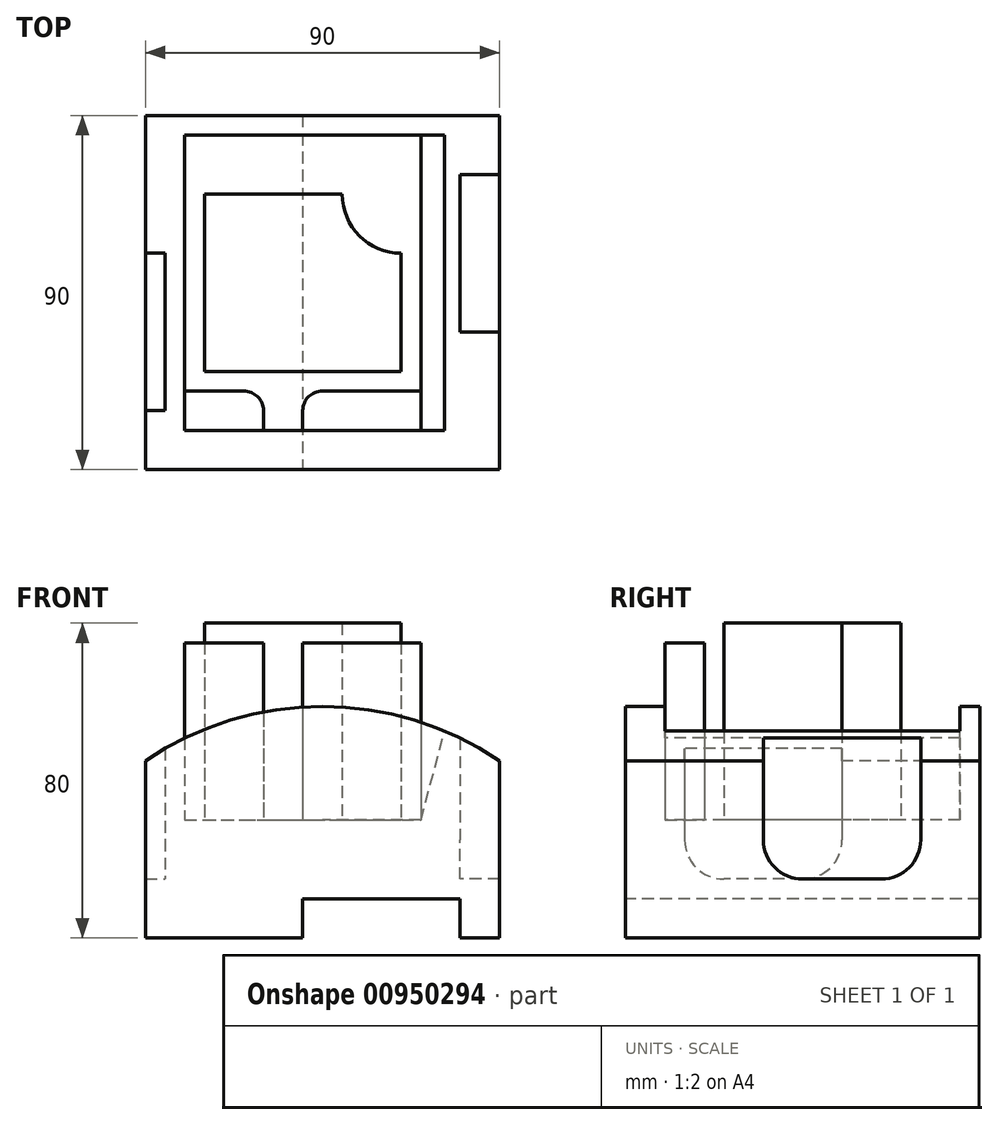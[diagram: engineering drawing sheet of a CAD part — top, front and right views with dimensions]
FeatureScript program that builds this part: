
annotation { "Feature Type Name" : "Feature", "Feature Type Description" : "" }
export const myFeature = defineFeature(function(context is Context, id is Id, definition is map)
    precondition{}
    {
        {
            var Q0;
            Q0=qCreatedBy(makeId("Front.planeOp"),FACE);
            var sketch = newSketch(context, id + "F0", { "sketchPlane" : qUnion([Q0])});
            skLineSegment(sketch, "E0", {"start": v(0, 45) * mm, "end": v(0, 0) * mm});
            skLineSegment(sketch, "E1", {"start": v(0, 0) * mm, "end": v(40, 0) * mm});
            skLineSegment(sketch, "E2", {"start": v(40, 0) * mm, "end": v(40, 10) * mm});
            skLineSegment(sketch, "E3", {"start": v(40, 10) * mm, "end": v(80, 10) * mm});
            skLineSegment(sketch, "E4", {"start": v(80, 10) * mm, "end": v(80, 0) * mm});
            skLineSegment(sketch, "E5", {"start": v(80, 0) * mm, "end": v(90, 0) * mm});
            skLineSegment(sketch, "E6", {"start": v(90, 0) * mm, "end": v(90, 45) * mm});
            skArc(sketch, "E7", {"start": v(90, 45) * mm, "mid": v(45, 58.86) * mm, "end": v(0, 45) * mm});
            skSolve(sketch);
        }
        {
            var Q0;
            Q0 = qSketchRegion(id + "F0", true);
            extrude(context, id + "F1", {"entities" : qUnion([Q0]), "oppositeDirection" : true, "depth" : 90 * mm, "offsetDistance" : 25 * mm});
        }
        {
            var Q0;
            Q0=makeQuery(id+"F1.opExtrude","SWEPT_FACE",FACE,{"disambiguationData":[OSD([sQuery(id+"F0.wireOp",EDGE,"E1")])]});
            cPlane(context, id + "F2", {"entities" : qUnion([Q0]), "cplaneType" : CPlaneType.OFFSET, "offset" : 30 * mm, "oppositeDirection" : true, "width" : 150 * mm, "height" : 150 * mm});
        }
        {
            var Q0;
            Q0=qCreatedBy(id+"F2.planeOp",FACE);
            var sketch = newSketch(context, id + "F3", { "sketchPlane" : qUnion([Q0])});
            skLineSegment(sketch, "E8.bottom", {"start": v(10, -85) * mm, "end": v(70, -85) * mm});
            skLineSegment(sketch, "E8.top", {"start": v(10, -10) * mm, "end": v(70, -10) * mm});
            skLineSegment(sketch, "E8.left", {"start": v(10, -85) * mm, "end": v(10, -10) * mm});
            skLineSegment(sketch, "E8.right", {"start": v(70, -85) * mm, "end": v(70, -10) * mm});
            skSolve(sketch);
        }
        {
            var Q0;
            Q0 = qSketchRegion(id + "F3", true);
            extrude(context, id + "F4", {"entities" : qUnion([Q0]), "operationType" : NewBodyOperationType.REMOVE, "endBound" : BoundingType.THROUGH_ALL, "oppositeDirection" : true, "depth" : 25 * mm, "offsetDistance" : 25 * mm});
        }
        {
            var Q0;
            Q0=makeQuery(id+"F4.boolean.opBoolean","COPY",FACE,{"derivedFrom":makeQuery(id+"F4.opExtrude","SWEPT_FACE",FACE,{"disambiguationData":[OSD([sQuery(id+"F3.wireOp",EDGE,"E8.bottom")])]})});
            var sketch = newSketch(context, id + "F5", { "sketchPlane" : qUnion([Q0])});
            skLineSegment(sketch, "E9", {"start": v(70, 54.85) * mm, "end": v(70, 30) * mm});
            skLineSegment(sketch, "E10", {"start": v(70, 30) * mm, "end": v(76.66, 54.85) * mm});
            skLineSegment(sketch, "E11", {"start": v(76.66, 54.85) * mm, "end": v(70, 54.85) * mm});
            skSolve(sketch);
        }
        {
            var Q0;
            Q0 = qSketchRegion(id + "F5", true);
            var Q1;
            Q1=makeQuery(id+"F4.boolean.opBoolean","COPY",FACE,{"derivedFrom":makeQuery(id+"F4.opExtrude","SWEPT_FACE",FACE,{"disambiguationData":[OSD([sQuery(id+"F3.wireOp",EDGE,"E8.top")])]})});
            extrude(context, id + "F6", {"entities" : qUnion([Q0]), "operationType" : NewBodyOperationType.REMOVE, "endBound" : BoundingType.UP_TO_SURFACE, "depth" : 25 * mm, "endBoundEntityFace" : qUnion([Q1]), "offsetDistance" : 25 * mm});
        }
        {
            var Q0;
            Q0=makeQuery(id+"F4.boolean.opBoolean","COPY",FACE,{"derivedFrom":makeQuery(id+"F4.opExtrude","CAP_FACE",FACE,{"disambiguationData":[OSD([sQuery(id+"F3.wireOp",EDGE,"E8.bottom"),sQuery(id+"F3.wireOp",EDGE,"E8.top"),sQuery(id+"F3.wireOp",EDGE,"E8.left"),sQuery(id+"F3.wireOp",EDGE,"E8.right")])],"isStart":true})});
            var sketch = newSketch(context, id + "F7", { "sketchPlane" : qUnion([Q0])});
            skLineSegment(sketch, "E12.bottom", {"start": v(10, 10) * mm, "end": v(30, 10) * mm});
            skLineSegment(sketch, "E12.top", {"start": v(10, 20) * mm, "end": v(30, 20) * mm});
            skLineSegment(sketch, "E12.left", {"start": v(10, 10) * mm, "end": v(10, 20) * mm});
            skLineSegment(sketch, "E12.right", {"start": v(30, 10) * mm, "end": v(30, 20) * mm});
            skLineSegment(sketch, "E13.bottom", {"start": v(70, 10) * mm, "end": v(40, 10) * mm});
            skLineSegment(sketch, "E13.top", {"start": v(70, 20) * mm, "end": v(40, 20) * mm});
            skLineSegment(sketch, "E13.left", {"start": v(70, 10) * mm, "end": v(70, 20) * mm});
            skLineSegment(sketch, "E13.right", {"start": v(40, 10) * mm, "end": v(40, 20) * mm});
            skSolve(sketch);
        }
        {
            var Q0;
            Q0 = qSketchRegion(id + "F7", true);
            extrude(context, id + "F8", {"entities" : qUnion([Q0]), "operationType" : NewBodyOperationType.ADD, "depth" : 45 * mm, "offsetDistance" : 25 * mm});
        }
        {
            var Q0;
            Q0=makeQuery(id+"F8.opExtrude","SWEPT_EDGE",EDGE,{"disambiguationData":[OSD([sQuery(id+"F7.wireOp",EDGE,"E13.top"),sQuery(id+"F7.wireOp",EDGE,"E13.right")])]});
            var Q1;
            Q1=makeQuery(id+"F8.opExtrude","SWEPT_EDGE",EDGE,{"disambiguationData":[OSD([sQuery(id+"F7.wireOp",EDGE,"E12.top"),sQuery(id+"F7.wireOp",EDGE,"E12.right")])]});
            fillet(context, id + "F9", {"entities" : qUnion([Q0, Q1]), "radius" : 5 * mm, "tangentPropagation" : true, "allowEdgeOverflow" : false});
        }
        {
            var Q0;
            Q0=makeQuery(id+"F4.boolean.opBoolean","COPY",FACE,{"derivedFrom":makeQuery(id+"F4.opExtrude","CAP_FACE",FACE,{"disambiguationData":[OSD([sQuery(id+"F3.wireOp",EDGE,"E8.bottom"),sQuery(id+"F3.wireOp",EDGE,"E8.top"),sQuery(id+"F3.wireOp",EDGE,"E8.left"),sQuery(id+"F3.wireOp",EDGE,"E8.right")])],"isStart":true})});
            var sketch = newSketch(context, id + "F10", { "sketchPlane" : qUnion([Q0])});
            skLineSegment(sketch, "E14.bottom", {"start": v(15, 70) * mm, "end": v(50, 70) * mm});
            skLineSegment(sketch, "E14.top", {"start": v(15, 25) * mm, "end": v(65, 25) * mm});
            skLineSegment(sketch, "E14.left", {"start": v(15, 70) * mm, "end": v(15, 25) * mm});
            skLineSegment(sketch, "E14.right", {"start": v(65, 55) * mm, "end": v(65, 25) * mm});
            skArc(sketch, "E15", {"start": v(50, 70) * mm, "mid": v(54.4, 59.4) * mm, "end": v(65, 55) * mm});
            skSolve(sketch);
        }
        {
            var Q0;
            Q0 = qSketchRegion(id + "F10", true);
            extrude(context, id + "F11", {"entities" : qUnion([Q0]), "operationType" : NewBodyOperationType.ADD, "depth" : 50 * mm, "offsetDistance" : 25 * mm});
        }
        {
            var Q0;
            Q0=makeQuery(id+"F1.opExtrude","SWEPT_FACE",FACE,{"disambiguationData":[OSD([sQuery(id+"F0.wireOp",EDGE,"E1")])]});
            cPlane(context, id + "F12", {"entities" : qUnion([Q0]), "cplaneType" : CPlaneType.OFFSET, "offset" : 15 * mm, "oppositeDirection" : true, "width" : 150 * mm, "height" : 150 * mm});
        }
        {
            var Q0;
            Q0=qCreatedBy(id+"F12.planeOp",FACE);
            var sketch = newSketch(context, id + "F13", { "sketchPlane" : qUnion([Q0])});
            skLineSegment(sketch, "E16.bottom", {"start": v(0, -55) * mm, "end": v(5, -55) * mm});
            skLineSegment(sketch, "E16.top", {"start": v(0, -15) * mm, "end": v(5, -15) * mm});
            skLineSegment(sketch, "E16.left", {"start": v(0, -55) * mm, "end": v(0, -15) * mm});
            skLineSegment(sketch, "E16.right", {"start": v(5, -55) * mm, "end": v(5, -15) * mm});
            skLineSegment(sketch, "E17.bottom", {"start": v(90, -75) * mm, "end": v(80, -75) * mm});
            skLineSegment(sketch, "E17.top", {"start": v(90, -35) * mm, "end": v(80, -35) * mm});
            skLineSegment(sketch, "E17.left", {"start": v(90, -75) * mm, "end": v(90, -35) * mm});
            skLineSegment(sketch, "E17.right", {"start": v(80, -75) * mm, "end": v(80, -35) * mm});
            skSolve(sketch);
        }
        {
            var Q0;
            Q0 = qSketchRegion(id + "F13", true);
            extrude(context, id + "F14", {"entities" : qUnion([Q0]), "operationType" : NewBodyOperationType.REMOVE, "endBound" : BoundingType.THROUGH_ALL, "oppositeDirection" : true, "depth" : 25 * mm, "offsetDistance" : 25 * mm});
        }
        {
            var Q0;
            Q0=makeQuery(id+"F14.boolean.opBoolean","COPY",EDGE,{"derivedFrom":makeQuery(id+"F14.opExtrude","CAP_EDGE",EDGE,{"disambiguationData":[OSD([sQuery(id+"F13.wireOp",EDGE,"E16.bottom")])],"isStart":true})});
            var Q1;
            Q1=makeQuery(id+"F14.boolean.opBoolean","COPY",EDGE,{"derivedFrom":makeQuery(id+"F14.opExtrude","CAP_EDGE",EDGE,{"disambiguationData":[OSD([sQuery(id+"F13.wireOp",EDGE,"E16.top")])],"isStart":true})});
            var Q2;
            Q2=makeQuery(id+"F14.boolean.opBoolean","COPY",EDGE,{"derivedFrom":makeQuery(id+"F14.opExtrude","CAP_EDGE",EDGE,{"disambiguationData":[OSD([sQuery(id+"F13.wireOp",EDGE,"E17.top")])],"isStart":true})});
            var Q3;
            Q3=makeQuery(id+"F14.boolean.opBoolean","COPY",EDGE,{"derivedFrom":makeQuery(id+"F14.opExtrude","CAP_EDGE",EDGE,{"disambiguationData":[OSD([sQuery(id+"F13.wireOp",EDGE,"E17.bottom")])],"isStart":true})});
            fillet(context, id + "F15", {"entities" : qUnion([Q0, Q1, Q2, Q3]), "radius" : 10 * mm, "tangentPropagation" : true, "allowEdgeOverflow" : false});
        }
    });
